FCSTD DOCUMENT  (FreeCAD 0.16R)
Label: HeadLightBracket
License: All rights reserved
LicenseURL: http://en.wikipedia.org/wiki/All_rights_reserved
objects: Sketcher::SketchObject×5, PartDesign::Pocket×4, PartDesign::Chamfer×2, PartDesign::Pad×1, PartDesign::Fillet×1, Mesh::Feature×1
note: 18 computed .brp shape members not serialized (recipe doc carries the construction recipe); baked Part::Feature solids carry a one-line shape summary decoded from their .brp

FEATURE [Sketcher::SketchObject] Sketch
  sketch-geometry (4):
    g0: LineSegment StartX=-30 StartY=10 StartZ=0 EndX=30 EndY=10 EndZ=0
    g1: LineSegment StartX=30 StartY=10 StartZ=0 EndX=30 EndY=-10 EndZ=0
    g2: LineSegment StartX=30 StartY=-10 StartZ=0 EndX=-30 EndY=-10 EndZ=0
    g3: LineSegment StartX=-30 StartY=-10 StartZ=0 EndX=-30 EndY=10 EndZ=0
  constraints (11):
    c: Coincident(g0,g1)
    c: Coincident(g1,g2)
    c: Coincident(g2,g3)
    c: Coincident(g3,g0)
    c: Horizontal(g0)
    c: Horizontal(g2)
    c: Vertical(g1)
    c: Vertical(g3)
    c: Symmetric(g0,g2,g-1)
    c: Distance(g0) = 60
    c: Distance(g1) = 20
FEATURE [PartDesign::Pad] Pad
  Length = 35
  Length2 = 100
  Sketch = -> Sketch
  Type = 0
FEATURE [Sketcher::SketchObject] Sketch001
  ExternalGeometry = -> [Pad]
  Placement = pos=(0,10,0) rot=(0,0.707107,0.707107;3.14159rad)
  Support = -> Pad [Face1]
  sketch-geometry (1):
    g0: Circle CenterX=0 CenterY=35 CenterZ=0 NormalX=0 NormalY=0 NormalZ=1 Radius=20.75
  constraints (2):
    c: Radius(g0) = 20.75
    c: Symmetric(g-6,g-6,g0)
FEATURE [PartDesign::Pocket] Pocket
  Length = 9
  Sketch = -> Sketch001
  Type = 1
FEATURE [Sketcher::SketchObject] Sketch002
  ExternalGeometry = -> [Pocket]
  Placement = pos=(0,0,35) rot=(0,0,1;0rad)
  Support = -> Pocket [Face4]
  sketch-geometry (2):
    g0: Circle CenterX=-25 CenterY=0 CenterZ=0 NormalX=0 NormalY=0 NormalZ=1 Radius=1.9
    g1: Circle CenterX=25 CenterY=0 CenterZ=0 NormalX=0 NormalY=0 NormalZ=1 Radius=1.9
  constraints (6):
    c: Radius(g1) = 1.9
    c: Equal(g1,g0)
    c: DistanceX(g-1,g1) = 25
    c: Distance(g-1,g0) = 25
    c: PointOnObject(g0,g-1)
    c: PointOnObject(g1,g-1)
FEATURE [PartDesign::Pocket] Pocket001
  Length = 15
  Sketch = -> Sketch002
  Type = 0
FEATURE [Sketcher::SketchObject] Sketch003
  ExternalGeometry = -> [Pocket001]
  Placement = pos=(0,0,35) rot=(0,0,1;0rad)
  Support = -> Pocket001 [Face6]
  sketch-geometry (1):
    g0: Circle CenterX=0 CenterY=0 CenterZ=0 NormalX=0 NormalY=0 NormalZ=1 Radius=3.15
  constraints (2):
    c: Coincident(g0,g-1)
    c: Radius(g0) = 3.15
FEATURE [PartDesign::Pocket] Pocket002
  Length = 5
  Sketch = -> Sketch003
  Type = 1
FEATURE [Sketcher::SketchObject] Sketch004
  Placement = pos=(0,0,35) rot=(0,0,1;0rad)
  Support = -> Pocket002 [Face6]
  sketch-geometry (7):
    g0: LineSegment StartX=3.9e-11 StartY=-6.06218 StartZ=0 EndX=5.25 EndY=-3.03109 EndZ=0
    g1: LineSegment StartX=5.25 StartY=-3.03109 StartZ=0 EndX=5.25 EndY=3.03109 EndZ=0
    g2: LineSegment StartX=5.25 StartY=3.03109 StartZ=0 EndX=0 EndY=6.06218 EndZ=0
    g3: LineSegment StartX=0 StartY=6.06218 StartZ=0 EndX=-5.25 EndY=3.03109 EndZ=0
    g4: LineSegment StartX=-5.25 StartY=3.03109 StartZ=0 EndX=-5.25 EndY=-3.03109 EndZ=0
    g5: LineSegment StartX=-5.25 StartY=-3.03109 StartZ=0 EndX=3.9e-11 EndY=-6.06218 EndZ=0
    g6: Circle [constr] CenterX=0 CenterY=0 CenterZ=0 NormalX=0 NormalY=0 NormalZ=1 Radius=6.06218
  constraints (16):
    c: Coincident(g0,g1)
    c: Coincident(g1,g2)
    c: Coincident(g2,g3)
    c: Coincident(g3,g4)
    c: Coincident(g4,g5)
    c: Coincident(g5,g0)
    c: Equal(g0, g1-g5) x5
    c: PointOnObject(g0,g6)
    c: PointOnObject(g1,g6)
    c: PointOnObject(g2,g6)
    c: PointOnObject(g3,g6)
    c: PointOnObject(g4,g6)
    c: PointOnObject(g5,g6)
    c: Distance(g4,g2) = 10.5
    c: Coincident(g6,g-1)
    c: PointOnObject(g2,g-2)
FEATURE [PartDesign::Pocket] Pocket003
  Length = 26
  Sketch = -> Sketch004
  Type = 0
FEATURE [PartDesign::Chamfer] Chamfer
  Base = -> Pocket003 [Edge8,Edge7]
  Size = 15
FEATURE [PartDesign::Fillet] Fillet
  Base = -> Chamfer [Edge14,Edge9,Edge10,Edge15]
  Radius = 4
FEATURE [PartDesign::Chamfer] Chamfer001
  Base = -> Fillet [Edge1,Edge2,Edge3,Edge4,Edge5,Edge6,Edge7,Edge8,Edge9,Edge10,Edge11,Edge12,Edge15,Edge20,Edge17,Edge24,Edge21,Edge28,Edge25,Edge32,Edge29,Edge37,Edge33,Edge39]
  Size = 2
FEATURE [Mesh::Feature] Mesh  label="Chamfer001 (Meshed)"
